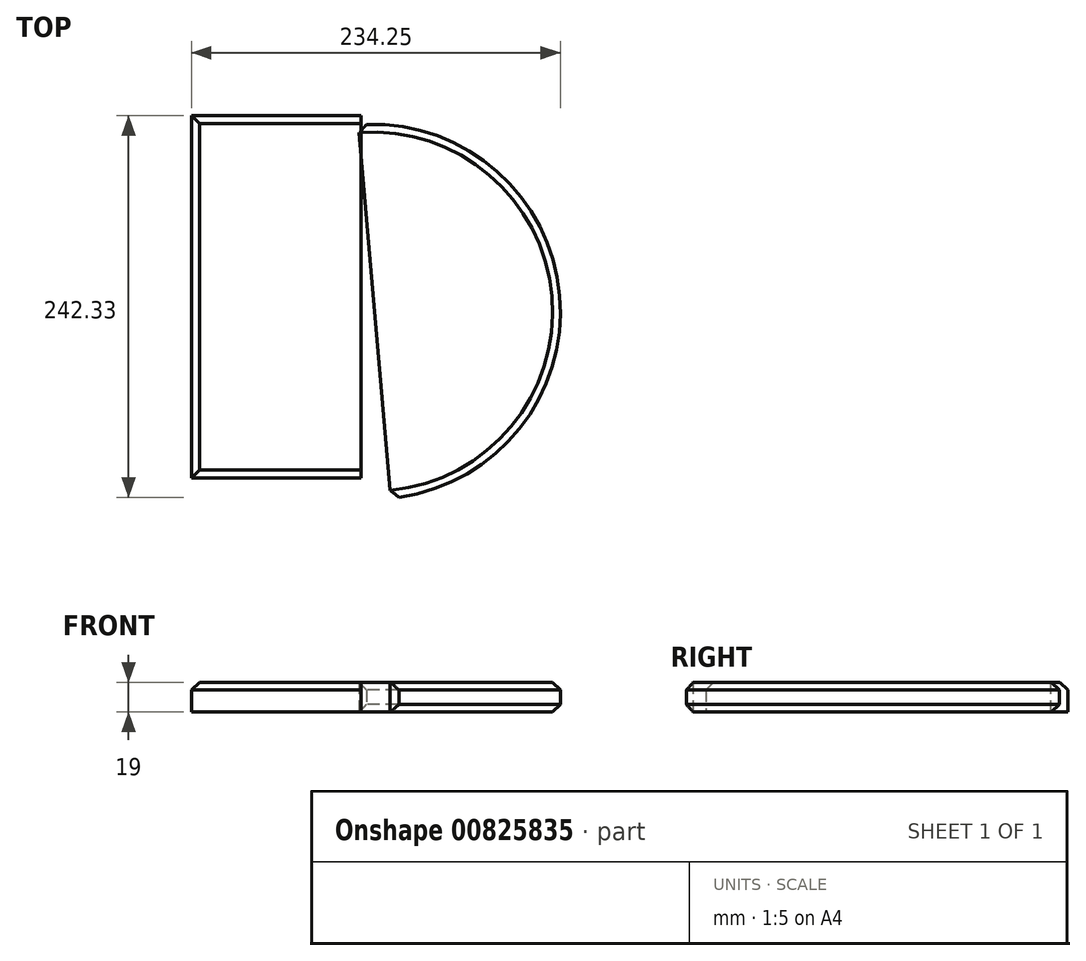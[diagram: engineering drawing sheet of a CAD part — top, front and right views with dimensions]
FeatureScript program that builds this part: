
annotation { "Feature Type Name" : "Feature", "Feature Type Description" : "" }
export const myFeature = defineFeature(function(context is Context, id is Id, definition is map)
    precondition{}
    {
        {
            var Q0;
            Q0=qCreatedBy(makeId("Top.planeOp"),FACE);
            var sketch = newSketch(context, id + "F0", { "sketchPlane" : qUnion([Q0])});
            skArc(sketch, "E0", {"start": v(11.22, -118.46) * mm, "mid": v(118.55, 10.29) * mm, "end": v(-9.36, 118.63) * mm});
            skLineSegment(sketch, "E1", {"start": v(-9.36, 118.63) * mm, "end": v(11.22, -118.46) * mm});
            skSolve(sketch);
        }
        {
            var Q0;
            Q0=qCreatedBy(makeId("Top.planeOp"),FACE);
            var sketch = newSketch(context, id + "F1", { "sketchPlane" : qUnion([Q0])});
            skLineSegment(sketch, "E2.bottom", {"start": v(-115.26, 124.48) * mm, "end": v(-7.54, 124.48) * mm});
            skLineSegment(sketch, "E2.top", {"start": v(-115.26, -105.52) * mm, "end": v(-7.54, -105.52) * mm});
            skLineSegment(sketch, "E2.left", {"start": v(-115.26, 124.48) * mm, "end": v(-115.26, -105.52) * mm});
            skLineSegment(sketch, "E2.right", {"start": v(-7.54, 124.48) * mm, "end": v(-7.54, -105.52) * mm});
            skSolve(sketch);
        }
        {
            var Q0;
            Q0=makeQuery(id+"F0.imprint","IMPRINT",FACE,{"disambiguationData":[TD([[makeQuery(id+"F0.imprint","IMPRINT",EDGE,{"derivedFrom":sQuery(id+"F0.wireOp",EDGE,"E0")}),1.0]])]});
            var Q1;
            Q1=makeQuery(id+"F1.imprint","IMPRINT",FACE,{"disambiguationData":[TD([[makeQuery(id+"F1.imprint","IMPRINT",EDGE,{"derivedFrom":sQuery(id+"F1.wireOp",EDGE,"E2.bottom")}),-1.0]])]});
            extrude(context, id + "F2", {"entities" : qUnion([Q0, Q1]), "depth" : 19 * mm, "offsetDistance" : 25 * mm});
        }
        {
            var Q0;
            Q0=makeQuery(id+"F2.opExtrude","CAP_EDGE",EDGE,{"disambiguationData":[OSD([sQuery(id+"F1.wireOp",EDGE,"E2.left")])],"isStart":false});
            chamfer(context, id + "F3", {"entities" : qUnion([Q0]), "width" : 5 * mm, "tangentPropagation" : true});
        }
        {
            var Q0;
            Q0=makeQuery(id+"F2.opExtrude","CAP_EDGE",EDGE,{"disambiguationData":[OSD([sQuery(id+"F1.wireOp",EDGE,"E2.top")])],"isStart":false});
            var Q1;
            Q1=makeQuery(id+"F2.opExtrude","SWEPT_FACE",FACE,{"disambiguationData":[OSD([sQuery(id+"F0.wireOp",EDGE,"E0")])]});
            var Q2;
            Q2=makeQuery(id+"F2.opExtrude","CAP_EDGE",EDGE,{"disambiguationData":[OSD([sQuery(id+"F1.wireOp",EDGE,"E2.bottom")])],"isStart":false});
            chamfer(context, id + "F4", {"entities" : qUnion([Q0, Q1, Q2]), "width" : 5 * mm, "tangentPropagation" : true});
        }
    });
